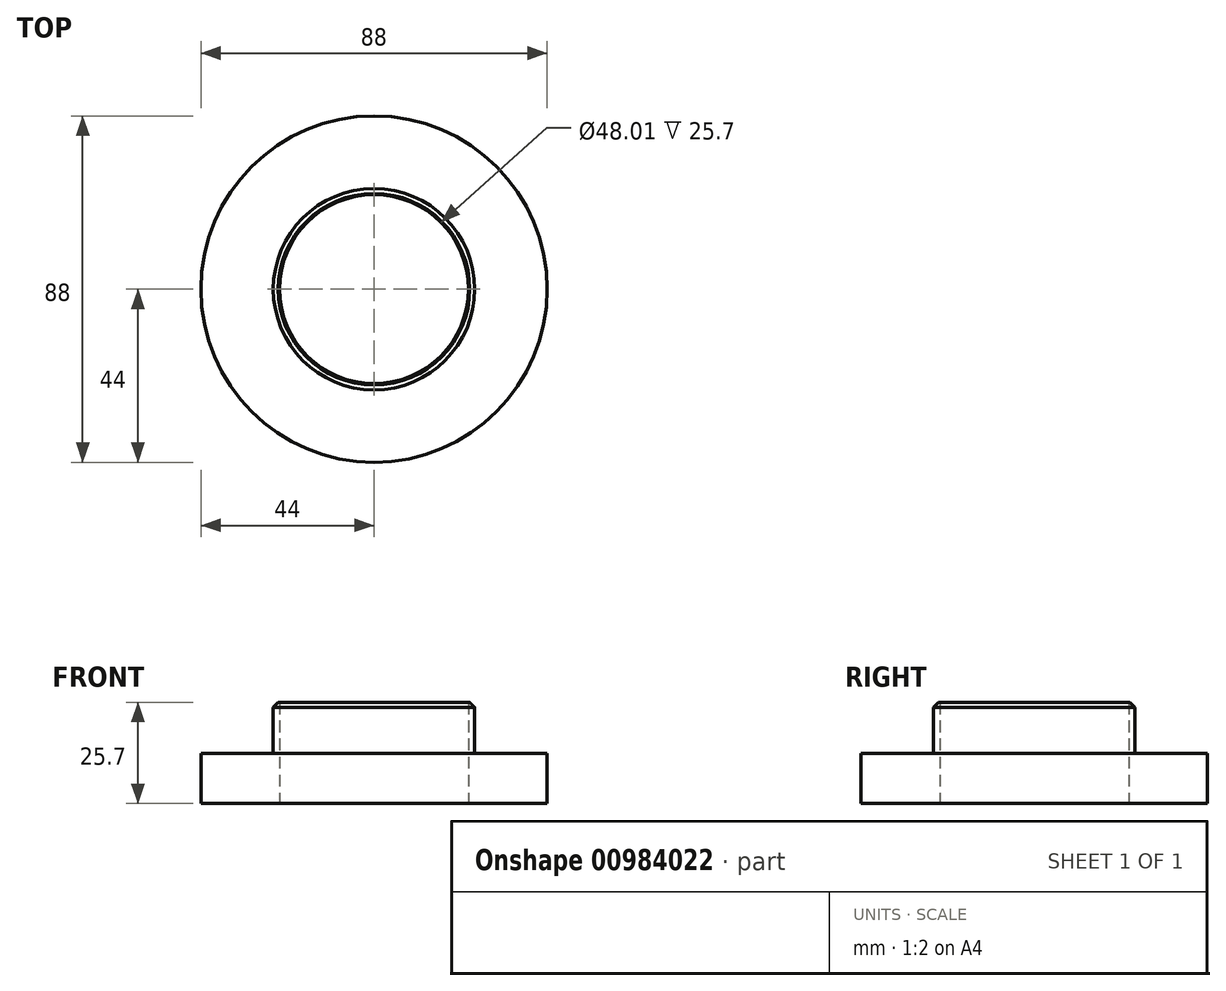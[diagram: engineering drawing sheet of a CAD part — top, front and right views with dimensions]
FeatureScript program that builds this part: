
annotation { "Feature Type Name" : "Feature", "Feature Type Description" : "" }
export const myFeature = defineFeature(function(context is Context, id is Id, definition is map)
    precondition{}
    {
        {
            var Q0;
            Q0=qCreatedBy(makeId("Top.planeOp"),FACE);
            var sketch = newSketch(context, id + "F0", { "sketchPlane" : qUnion([Q0])});
            skCircle(sketch, "E0", {"center": v(0, 0) * mm, "radius": 44 * mm});
            skCircle(sketch, "E1", {"center": v(0, 0) * mm, "radius": 24 * mm});
            skSolve(sketch);
        }
        {
            var Q0;
            Q0=makeQuery(id+"F0.imprint","IMPRINT",FACE,{"disambiguationData":[TD([[makeQuery(id+"F0.imprint","IMPRINT",EDGE,{"derivedFrom":sQuery(id+"F0.wireOp",EDGE,"E0")}),1.0]])]});
            extrude(context, id + "F1", {"entities" : qUnion([Q0]), "depth" : 12.7 * mm, "offsetDistance" : 25.4 * mm});
        }
        {
            var Q0;
            Q0=makeQuery(id+"F1.opExtrude","CAP_FACE",FACE,{"disambiguationData":[OSD([sQuery(id+"F0.wireOp",EDGE,"E0"),sQuery(id+"F0.wireOp",EDGE,"E1")])],"isStart":false});
            var sketch = newSketch(context, id + "F2", { "sketchPlane" : qUnion([Q0])});
            skCircle(sketch, "E2", {"center": v(0, 0) * mm, "radius": 25.6 * mm});
            skSolve(sketch);
        }
        {
            var Q0;
            Q0=makeQuery(id+"F2.imprint","IMPRINT",FACE,{"disambiguationData":[TD([[makeQuery(id+"F2.imprint","IMPRINT",EDGE,{"derivedFrom":sQuery(id+"F2.wireOp",EDGE,"E2")}),1.0]])]});
            extrude(context, id + "F3", {"entities" : qUnion([Q0]), "operationType" : NewBodyOperationType.ADD, "depth" : 13 * mm, "offsetDistance" : 25.4 * mm});
        }
        {
            var Q0;
            Q0=makeQuery(id+"F3.opExtrude","CAP_EDGE",EDGE,{"disambiguationData":[OSD([sQuery(id+"F2.wireOp",EDGE,"E2")])],"isStart":false});
            chamfer(context, id + "F4", {"entities" : qUnion([Q0]), "width" : 1.27 * mm, "tangentPropagation" : true});
        }
    });
